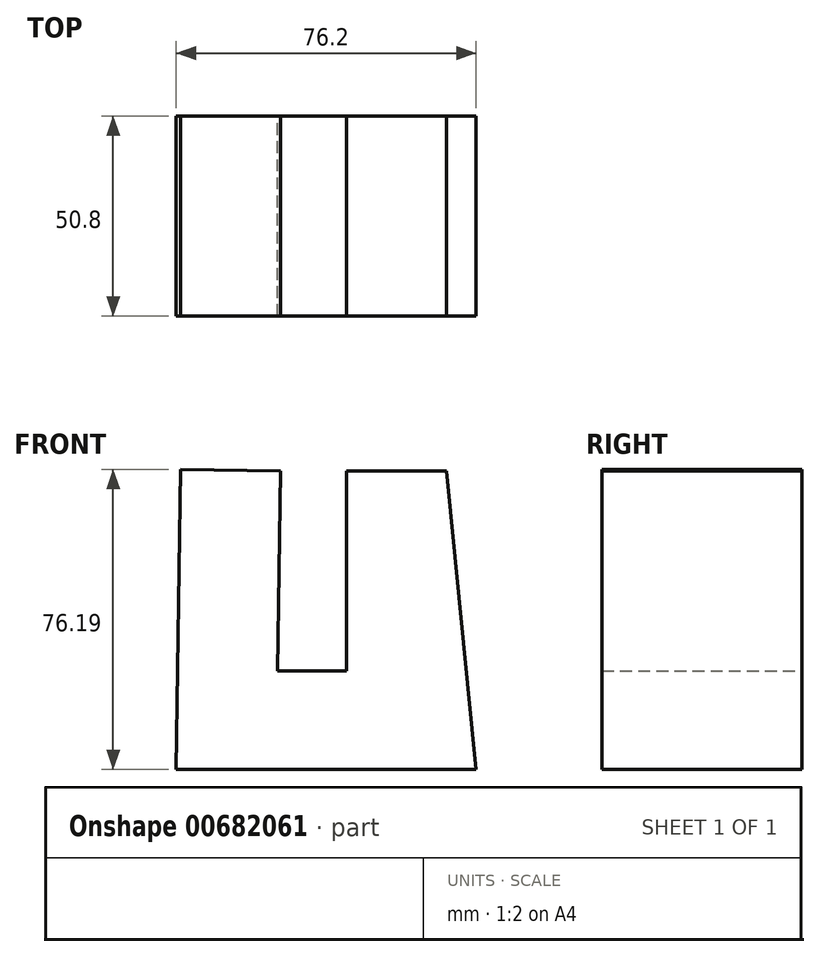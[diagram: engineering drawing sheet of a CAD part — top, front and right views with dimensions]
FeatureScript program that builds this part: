
annotation { "Feature Type Name" : "Feature", "Feature Type Description" : "" }
export const myFeature = defineFeature(function(context is Context, id is Id, definition is map)
    precondition{}
    {
        {
            var Q0;
            Q0=qCreatedBy(makeId("Front.planeOp"),FACE);
            var sketch = newSketch(context, id + "F0", { "sketchPlane" : qUnion([Q0])});
            skLineSegment(sketch, "E0", {"start": v(-29.24, 33.91) * mm, "end": v(-30.33, -42.28) * mm});
            skLineSegment(sketch, "E1", {"start": v(-30.33, -42.28) * mm, "end": v(45.87, -42.28) * mm});
            skLineSegment(sketch, "E2", {"start": v(-29.24, 33.91) * mm, "end": v(-3.84, 33.55) * mm});
            skLineSegment(sketch, "E3", {"start": v(-3.84, 33.55) * mm, "end": v(-4.57, -17.25) * mm});
            skLineSegment(sketch, "E4", {"start": v(-4.57, -17.25) * mm, "end": v(13, -17.25) * mm});
            skLineSegment(sketch, "E5", {"start": v(13, -17.25) * mm, "end": v(13, 33.55) * mm});
            skLineSegment(sketch, "E6", {"start": v(13, 33.55) * mm, "end": v(38.4, 33.55) * mm});
            skLineSegment(sketch, "E7", {"start": v(38.4, 33.55) * mm, "end": v(45.87, -42.28) * mm});
            skSolve(sketch);
        }
        {
            var Q0;
            Q0 = qSketchRegion(id + "F0", true);
            extrude(context, id + "F1", {"entities" : qUnion([Q0]), "depth" : 50.8 * mm, "offsetDistance" : 25.4 * mm});
        }
    });
